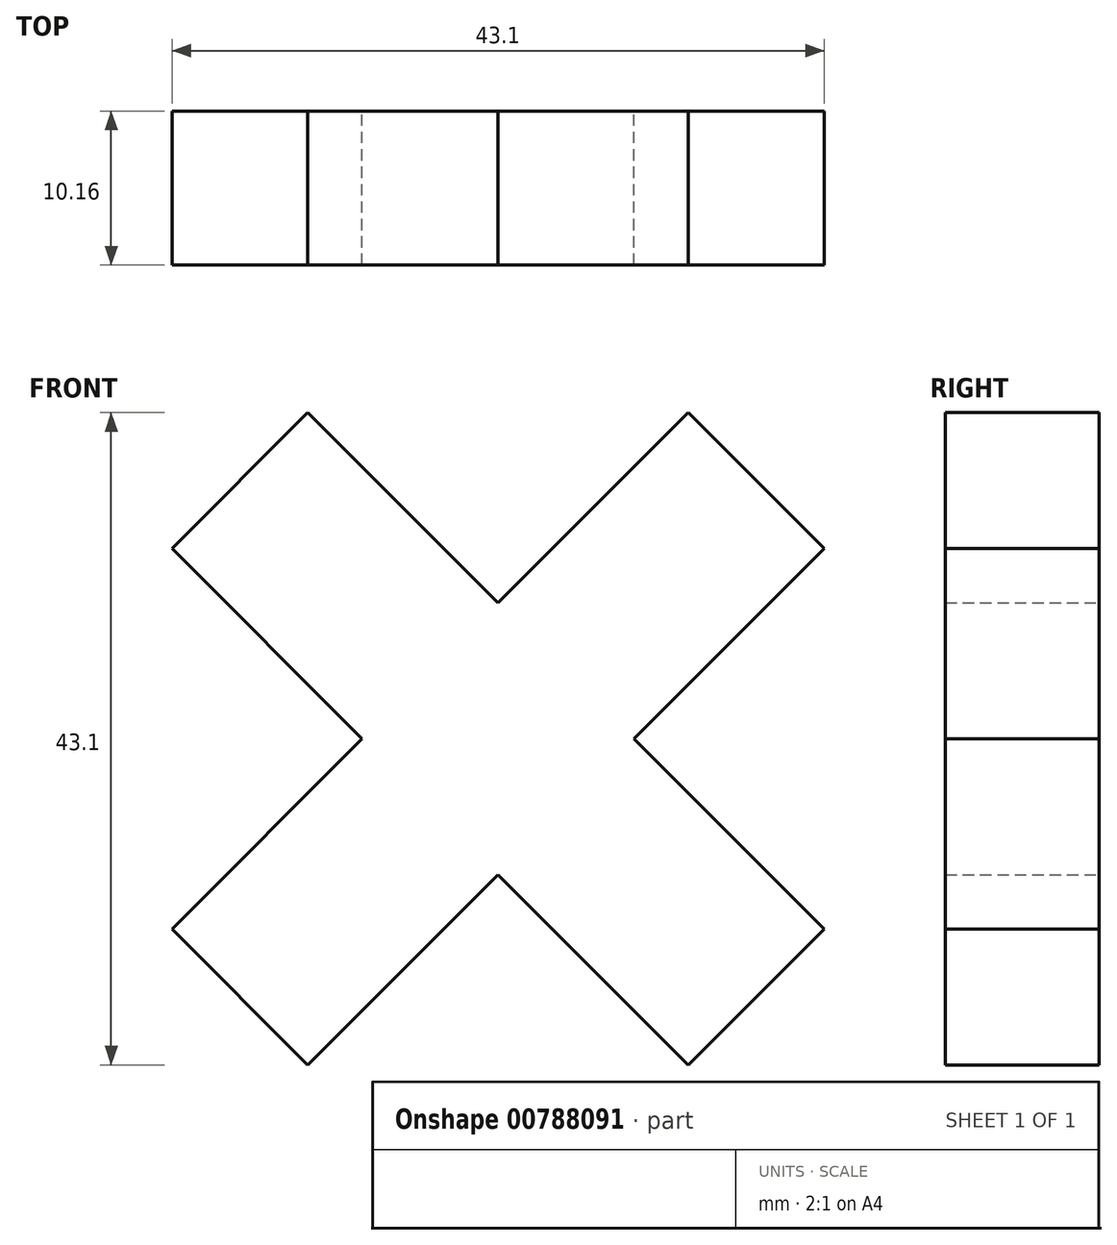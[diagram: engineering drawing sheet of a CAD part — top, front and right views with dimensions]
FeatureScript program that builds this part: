
annotation { "Feature Type Name" : "Feature", "Feature Type Description" : "" }
export const myFeature = defineFeature(function(context is Context, id is Id, definition is map)
    precondition{}
    {
        {
            var Q0;
            Q0=qCreatedBy(makeId("Front.planeOp"),FACE);
            var sketch = newSketch(context, id + "F0", { "sketchPlane" : qUnion([Q0])});
            skLineSegment(sketch, "E0", {"start": v(-49.27, 0) * mm, "end": v(-61.84, 12.57) * mm});
            skLineSegment(sketch, "E1", {"start": v(-61.84, 12.57) * mm, "end": v(-52.86, 21.55) * mm});
            skLineSegment(sketch, "E2", {"start": v(-52.86, 21.55) * mm, "end": v(-40.29, 8.98) * mm});
            skLineSegment(sketch, "E3", {"start": v(-40.29, 8.98) * mm, "end": v(-27.72, 21.55) * mm});
            skLineSegment(sketch, "E4", {"start": v(-27.72, 21.55) * mm, "end": v(-18.74, 12.57) * mm});
            skLineSegment(sketch, "E5", {"start": v(-18.74, 12.57) * mm, "end": v(-31.3, 0) * mm});
            skLineSegment(sketch, "E6", {"start": v(-31.3, 0) * mm, "end": v(-18.74, -12.57) * mm});
            skLineSegment(sketch, "E7", {"start": v(-18.74, -12.57) * mm, "end": v(-27.72, -21.55) * mm});
            skLineSegment(sketch, "E8", {"start": v(-27.72, -21.55) * mm, "end": v(-40.29, -8.98) * mm});
            skLineSegment(sketch, "E9", {"start": v(-40.29, -8.98) * mm, "end": v(-52.86, -21.55) * mm});
            skLineSegment(sketch, "E10", {"start": v(-52.86, -21.55) * mm, "end": v(-61.84, -12.57) * mm});
            skLineSegment(sketch, "E11", {"start": v(-61.84, -12.57) * mm, "end": v(-49.27, 0) * mm});
            skSolve(sketch);
        }
        {
            var Q0;
            Q0=makeQuery(id+"F0.imprint","IMPRINT",FACE,{"disambiguationData":[TD([[makeQuery(id+"F0.imprint","IMPRINT",EDGE,{"derivedFrom":sQuery(id+"F0.wireOp",EDGE,"E0")}),-1.0]])]});
            extrude(context, id + "F1", {"entities" : qUnion([Q0]), "depth" : 10.16 * mm, "offsetDistance" : 25.4 * mm});
        }
    });
